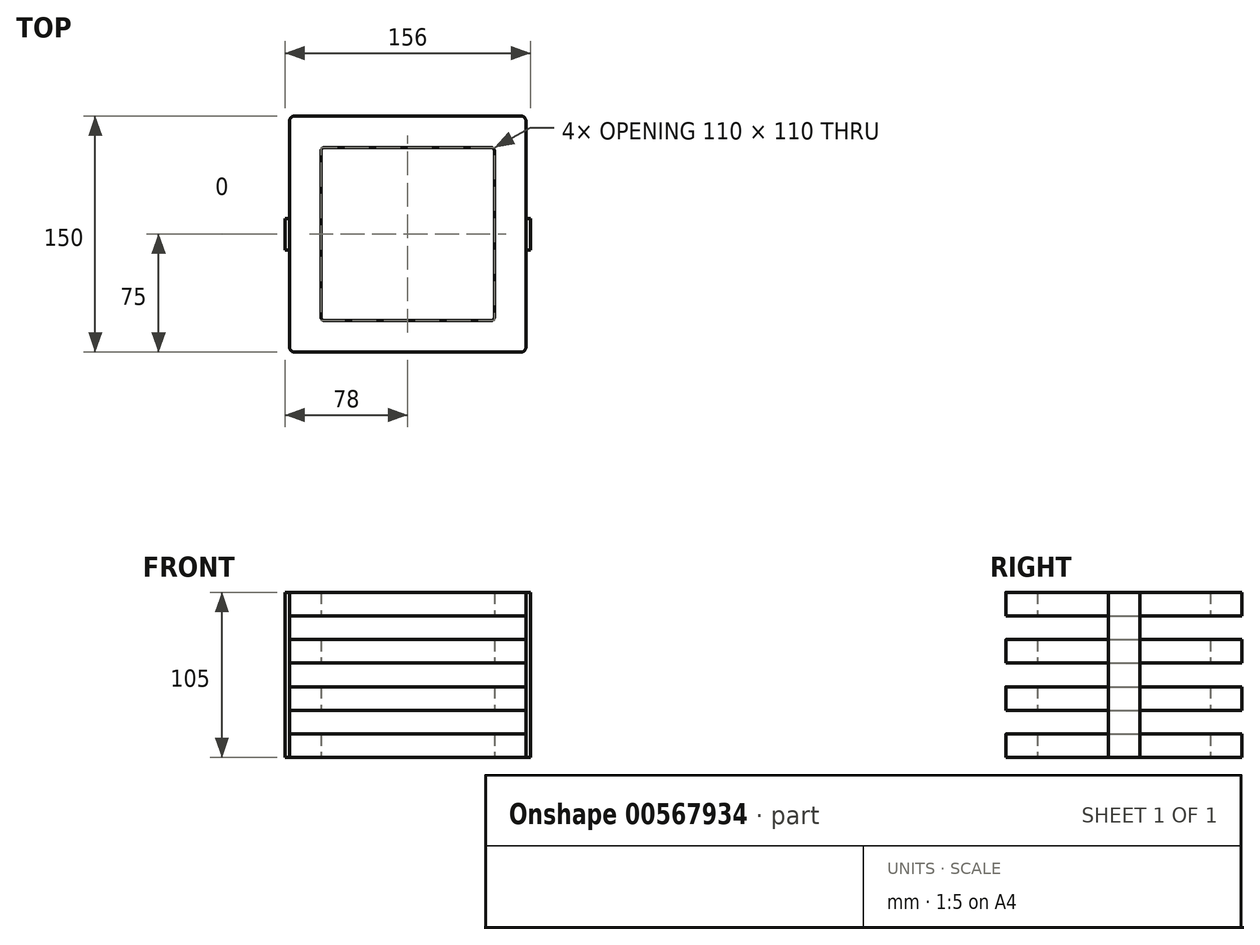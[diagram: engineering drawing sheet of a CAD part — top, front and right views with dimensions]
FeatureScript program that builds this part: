
annotation { "Feature Type Name" : "Feature", "Feature Type Description" : "" }
export const myFeature = defineFeature(function(context is Context, id is Id, definition is map)
    precondition{}
    {
        {
            var Q0;
            Q0=qCreatedBy(makeId("Top.planeOp"),FACE);
            var sketch = newSketch(context, id + "F0", { "sketchPlane" : qUnion([Q0])});
            skLineSegment(sketch, "E0.bottom", {"start": v(72, -75) * mm, "end": v(-72, -75) * mm});
            skLineSegment(sketch, "E0.top", {"start": v(72, 75) * mm, "end": v(-72, 75) * mm});
            skLineSegment(sketch, "E0.left", {"start": v(75, -72) * mm, "end": v(75, 72) * mm});
            skLineSegment(sketch, "E0.right", {"start": v(-75, -72) * mm, "end": v(-75, 72) * mm});
            skPoint(sketch, "E0.middle", {"position": v(0, 0) * mm});
            skPoint(sketch, "E1.visualSharp", {"position": v(-75, -75) * mm});
            skArc(sketch, "E1.filletArc", {"start": v(-75, -72) * mm, "mid": v(-74.12, -74.12) * mm, "end": v(-72, -75) * mm});
            skPoint(sketch, "E2.visualSharp", {"position": v(75, -75) * mm});
            skArc(sketch, "E2.filletArc", {"start": v(72, -75) * mm, "mid": v(74.12, -74.12) * mm, "end": v(75, -72) * mm});
            skPoint(sketch, "E3.visualSharp", {"position": v(75, 75) * mm});
            skArc(sketch, "E3.filletArc", {"start": v(75, 72) * mm, "mid": v(74.12, 74.12) * mm, "end": v(72, 75) * mm});
            skPoint(sketch, "E4.visualSharp", {"position": v(-75, 75) * mm});
            skArc(sketch, "E4.filletArc", {"start": v(-72, 75) * mm, "mid": v(-74.12, 74.12) * mm, "end": v(-75, 72) * mm});
            skLineSegment(sketch, "E5.0", {"start": v(-55, -53) * mm, "end": v(-55, 53) * mm});
            skLineSegment(sketch, "E5.1", {"start": v(53, -55) * mm, "end": v(-53, -55) * mm});
            skLineSegment(sketch, "E5.2", {"start": v(55, -53) * mm, "end": v(55, 53) * mm});
            skLineSegment(sketch, "E5.3", {"start": v(53, 55) * mm, "end": v(-53, 55) * mm});
            skPoint(sketch, "E6.visualSharp", {"position": v(-55, -55) * mm});
            skArc(sketch, "E6.filletArc", {"start": v(-55, -53) * mm, "mid": v(-54.41, -54.41) * mm, "end": v(-53, -55) * mm});
            skPoint(sketch, "E7.visualSharp", {"position": v(55, -55) * mm});
            skArc(sketch, "E7.filletArc", {"start": v(53, -55) * mm, "mid": v(54.41, -54.41) * mm, "end": v(55, -53) * mm});
            skPoint(sketch, "E8.visualSharp", {"position": v(55, 55) * mm});
            skArc(sketch, "E8.filletArc", {"start": v(55, 53) * mm, "mid": v(54.41, 54.41) * mm, "end": v(53, 55) * mm});
            skPoint(sketch, "E9.visualSharp", {"position": v(-55, 55) * mm});
            skArc(sketch, "E9.filletArc", {"start": v(-53, 55) * mm, "mid": v(-54.41, 54.41) * mm, "end": v(-55, 53) * mm});
            skSolve(sketch);
        }
        {
            var Q0;
            Q0 = qSketchRegion(id + "F0", true);
            extrude(context, id + "F1", {"entities" : qUnion([Q0]), "depth" : 15 * mm, "offsetDistance" : 25 * mm});
        }
        {
            var Q0;
            Q0=makeQuery(id+"F1.opExtrude","SWEPT_BODY",BODY,{"disambiguationData":[OSD([sQuery(id+"F0.wireOp",EDGE,"E0.bottom"),sQuery(id+"F0.wireOp",EDGE,"E0.top"),sQuery(id+"F0.wireOp",EDGE,"E0.left"),sQuery(id+"F0.wireOp",EDGE,"E0.right"),sQuery(id+"F0.wireOp",EDGE,"E1.filletArc"),sQuery(id+"F0.wireOp",EDGE,"E2.filletArc"),sQuery(id+"F0.wireOp",EDGE,"E3.filletArc"),sQuery(id+"F0.wireOp",EDGE,"E4.filletArc"),sQuery(id+"F0.wireOp",EDGE,"E5.0"),sQuery(id+"F0.wireOp",EDGE,"E5.1"),sQuery(id+"F0.wireOp",EDGE,"E5.2"),sQuery(id+"F0.wireOp",EDGE,"E5.3"),sQuery(id+"F0.wireOp",EDGE,"E6.filletArc"),sQuery(id+"F0.wireOp",EDGE,"E7.filletArc"),sQuery(id+"F0.wireOp",EDGE,"E8.filletArc"),sQuery(id+"F0.wireOp",EDGE,"E9.filletArc")])]});
            transform(context, id + "F2", {"entities" : qUnion([Q0]), "transformType" : TransformType.TRANSLATION_3D, "dx" : 0 * mm, "dy" : 0 * mm, "dz" : 30 * mm, "makeCopy" : true});
        }
        {
            var Q0;
            Q0=makeQuery(id+"F2.opPattern","COPY",BODY,{"derivedFrom":makeQuery(id+"F1.opExtrude","SWEPT_BODY",BODY,{"disambiguationData":[OSD([sQuery(id+"F0.wireOp",EDGE,"E0.bottom"),sQuery(id+"F0.wireOp",EDGE,"E0.top"),sQuery(id+"F0.wireOp",EDGE,"E0.left"),sQuery(id+"F0.wireOp",EDGE,"E0.right"),sQuery(id+"F0.wireOp",EDGE,"E1.filletArc"),sQuery(id+"F0.wireOp",EDGE,"E2.filletArc"),sQuery(id+"F0.wireOp",EDGE,"E3.filletArc"),sQuery(id+"F0.wireOp",EDGE,"E4.filletArc"),sQuery(id+"F0.wireOp",EDGE,"E5.0"),sQuery(id+"F0.wireOp",EDGE,"E5.1"),sQuery(id+"F0.wireOp",EDGE,"E5.2"),sQuery(id+"F0.wireOp",EDGE,"E5.3"),sQuery(id+"F0.wireOp",EDGE,"E6.filletArc"),sQuery(id+"F0.wireOp",EDGE,"E7.filletArc"),sQuery(id+"F0.wireOp",EDGE,"E8.filletArc"),sQuery(id+"F0.wireOp",EDGE,"E9.filletArc")])]}),"instanceName":"1"});
            transform(context, id + "F3", {"entities" : qUnion([Q0]), "transformType" : TransformType.TRANSLATION_3D, "dx" : 0 * mm, "dy" : 0 * mm, "dz" : 30 * mm, "makeCopy" : true});
        }
        {
            var Q0;
            Q0=makeQuery(id+"F3.opPattern","COPY",BODY,{"derivedFrom":makeQuery(id+"F2.opPattern","COPY",BODY,{"derivedFrom":makeQuery(id+"F1.opExtrude","SWEPT_BODY",BODY,{"disambiguationData":[OSD([sQuery(id+"F0.wireOp",EDGE,"E0.bottom"),sQuery(id+"F0.wireOp",EDGE,"E0.top"),sQuery(id+"F0.wireOp",EDGE,"E0.left"),sQuery(id+"F0.wireOp",EDGE,"E0.right"),sQuery(id+"F0.wireOp",EDGE,"E1.filletArc"),sQuery(id+"F0.wireOp",EDGE,"E2.filletArc"),sQuery(id+"F0.wireOp",EDGE,"E3.filletArc"),sQuery(id+"F0.wireOp",EDGE,"E4.filletArc"),sQuery(id+"F0.wireOp",EDGE,"E5.0"),sQuery(id+"F0.wireOp",EDGE,"E5.1"),sQuery(id+"F0.wireOp",EDGE,"E5.2"),sQuery(id+"F0.wireOp",EDGE,"E5.3"),sQuery(id+"F0.wireOp",EDGE,"E6.filletArc"),sQuery(id+"F0.wireOp",EDGE,"E7.filletArc"),sQuery(id+"F0.wireOp",EDGE,"E8.filletArc"),sQuery(id+"F0.wireOp",EDGE,"E9.filletArc")])]}),"instanceName":"1"}),"instanceName":"1"});
            transform(context, id + "F4", {"entities" : qUnion([Q0]), "transformType" : TransformType.TRANSLATION_3D, "dx" : 0 * mm, "dy" : 0 * mm, "dz" : 30 * mm, "makeCopy" : true});
        }
        {
            var Q0;
            Q0=makeQuery(id+"F4.opPattern","COPY",FACE,{"derivedFrom":makeQuery(id+"F3.opPattern","COPY",FACE,{"derivedFrom":makeQuery(id+"F2.opPattern","COPY",FACE,{"derivedFrom":makeQuery(id+"F1.opExtrude","SWEPT_FACE",FACE,{"disambiguationData":[OSD([sQuery(id+"F0.wireOp",EDGE,"E0.left")])]}),"instanceName":"1"}),"instanceName":"1"}),"instanceName":"1"});
            var sketch = newSketch(context, id + "F5", { "sketchPlane" : qUnion([Q0])});
            skLineSegment(sketch, "E10.bottom", {"start": v(-10, 105) * mm, "end": v(10, 105) * mm});
            skLineSegment(sketch, "E10.top", {"start": v(-10, 0) * mm, "end": v(10, 0) * mm});
            skLineSegment(sketch, "E10.left", {"start": v(-10, 105) * mm, "end": v(-10, 0) * mm});
            skLineSegment(sketch, "E10.right", {"start": v(10, 105) * mm, "end": v(10, 0) * mm});
            skSolve(sketch);
        }
        {
            var Q0;
            Q0 = qSketchRegion(id + "F5", true);
            extrude(context, id + "F6", {"entities" : qUnion([Q0]), "depth" : 3 * mm, "offsetDistance" : 25 * mm});
        }
        {
            var Q0;
            Q0=makeQuery(id+"F6.opExtrude","SWEPT_BODY",BODY,{"disambiguationData":[OSD([sQuery(id+"F5.wireOp",EDGE,"E10.bottom"),sQuery(id+"F5.wireOp",EDGE,"E10.top"),sQuery(id+"F5.wireOp",EDGE,"E10.left"),sQuery(id+"F5.wireOp",EDGE,"E10.right")])]});
            transform(context, id + "F7", {"entities" : qUnion([Q0]), "transformType" : TransformType.TRANSLATION_3D, "dx" : -153 * mm, "dy" : 0 * mm, "dz" : 0 * mm, "makeCopy" : true});
        }
    });
